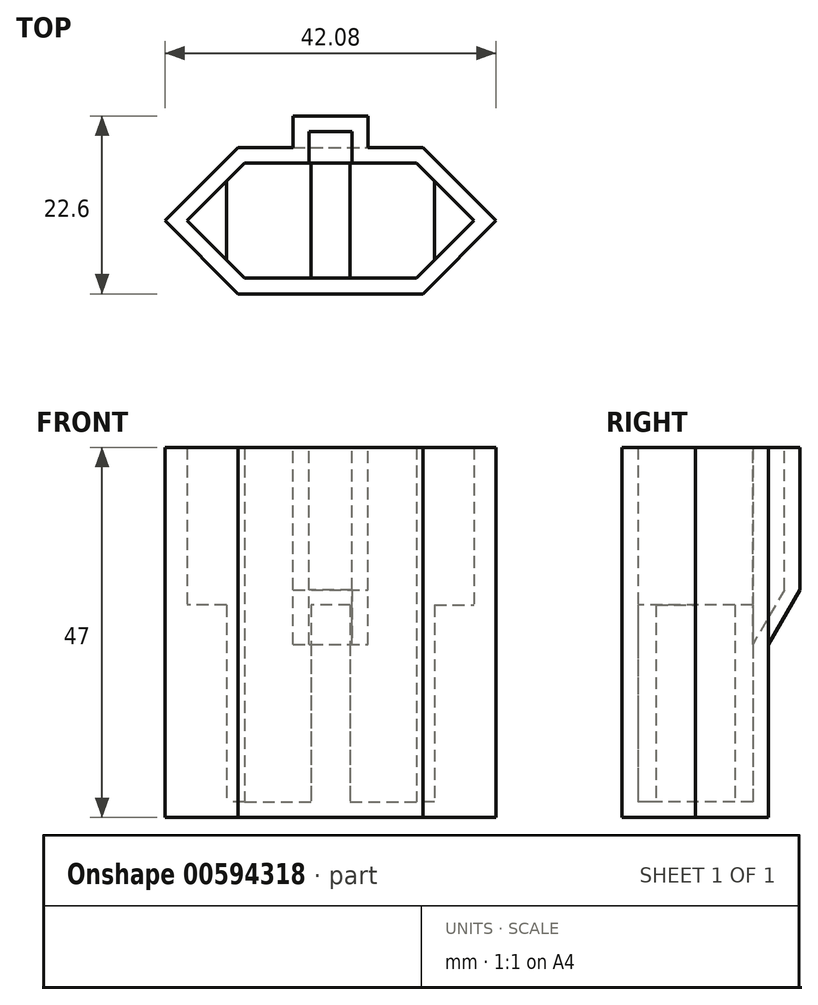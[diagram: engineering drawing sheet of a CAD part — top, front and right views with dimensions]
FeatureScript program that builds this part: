
annotation { "Feature Type Name" : "Feature", "Feature Type Description" : "" }
export const myFeature = defineFeature(function(context is Context, id is Id, definition is map)
    precondition{}
    {
        {
            var Q0;
            Q0=qCreatedBy(makeId("Top.planeOp"),FACE);
            var sketch = newSketch(context, id + "F0", { "sketchPlane" : qUnion([Q0])});
            skLineSegment(sketch, "E0", {"start": v(-10.7, 6.8) * mm, "end": v(10.7, 6.8) * mm, "construction": true});
            skLineSegment(sketch, "E1", {"start": v(10.7, 6.8) * mm, "end": v(17.5, 0) * mm, "construction": true});
            skLineSegment(sketch, "E2", {"start": v(17.5, 0) * mm, "end": v(10.7, -6.8) * mm, "construction": true});
            skLineSegment(sketch, "E3", {"start": v(10.7, -6.8) * mm, "end": v(-10.7, -6.8) * mm, "construction": true});
            skLineSegment(sketch, "E4", {"start": v(-10.7, -6.8) * mm, "end": v(-17.5, 0) * mm, "construction": true});
            skLineSegment(sketch, "E5", {"start": v(-17.5, 0) * mm, "end": v(-10.7, 6.8) * mm, "construction": true});
            skLineSegment(sketch, "E6.0", {"start": v(-10.9, -7.3) * mm, "end": v(-18.2, 0) * mm});
            skLineSegment(sketch, "E6.1", {"start": v(-10.9, 7.3) * mm, "end": v(10.9, 7.3) * mm});
            skLineSegment(sketch, "E6.2", {"start": v(10.9, 7.3) * mm, "end": v(18.2, 0) * mm});
            skLineSegment(sketch, "E6.3", {"start": v(-18.2, 0) * mm, "end": v(-10.9, 7.3) * mm});
            skLineSegment(sketch, "E6.4", {"start": v(18.2, 0) * mm, "end": v(10.9, -7.3) * mm});
            skLineSegment(sketch, "E6.5", {"start": v(10.9, -7.3) * mm, "end": v(-10.9, -7.3) * mm});
            skLineSegment(sketch, "E7.0", {"start": v(-21.04, 0) * mm, "end": v(-11.74, 9.3) * mm});
            skLineSegment(sketch, "E7.1", {"start": v(11.74, 9.3) * mm, "end": v(21.04, 0) * mm});
            skLineSegment(sketch, "E7.2", {"start": v(21.04, 0) * mm, "end": v(11.74, -9.3) * mm});
            skLineSegment(sketch, "E7.3", {"start": v(-11.74, 9.3) * mm, "end": v(11.74, 9.3) * mm});
            skLineSegment(sketch, "E7.4", {"start": v(11.74, -9.3) * mm, "end": v(-11.74, -9.3) * mm});
            skLineSegment(sketch, "E7.5", {"start": v(-11.74, -9.3) * mm, "end": v(-21.04, 0) * mm});
            skSolve(sketch);
        }
        {
            var Q0;
            Q0 = qSketchRegion(id + "F0", true);
            extrude(context, id + "F1", {"entities" : qUnion([Q0]), "depth" : 45 * mm, "offsetDistance" : 25 * mm});
        }
        {
            var Q0;
            Q0=makeQuery(id+"F1.opExtrude","CAP_FACE",FACE,{"disambiguationData":[OSD([sQuery(id+"F0.wireOp",EDGE,"E6.0"),sQuery(id+"F0.wireOp",EDGE,"E6.1"),sQuery(id+"F0.wireOp",EDGE,"E6.2"),sQuery(id+"F0.wireOp",EDGE,"E6.3"),sQuery(id+"F0.wireOp",EDGE,"E6.4"),sQuery(id+"F0.wireOp",EDGE,"E6.5"),sQuery(id+"F0.wireOp",EDGE,"E7.0"),sQuery(id+"F0.wireOp",EDGE,"E7.1"),sQuery(id+"F0.wireOp",EDGE,"E7.2"),sQuery(id+"F0.wireOp",EDGE,"E7.3"),sQuery(id+"F0.wireOp",EDGE,"E7.4"),sQuery(id+"F0.wireOp",EDGE,"E7.5")])],"isStart":false});
            var sketch = newSketch(context, id + "F2", { "sketchPlane" : qUnion([Q0])});
            skLineSegment(sketch, "E8.bottom", {"start": v(-2.75, 9.3) * mm, "end": v(2.75, 9.3) * mm});
            skLineSegment(sketch, "E8.top", {"start": v(-2.75, 7.3) * mm, "end": v(2.75, 7.3) * mm});
            skLineSegment(sketch, "E8.left", {"start": v(-2.75, 9.3) * mm, "end": v(-2.75, 7.3) * mm});
            skLineSegment(sketch, "E8.right", {"start": v(2.75, 9.3) * mm, "end": v(2.75, 7.3) * mm});
            skSolve(sketch);
        }
        {
            var Q0;
            Q0=makeQuery(id+"F2.imprint","IMPRINT",FACE,{"disambiguationData":[TD([[makeQuery(id+"F2.imprint","IMPRINT",EDGE,{"derivedFrom":sQuery(id+"F2.wireOp",EDGE,"E8.top")}),1.0]])]});
            extrude(context, id + "F3", {"entities" : qUnion([Q0]), "operationType" : NewBodyOperationType.REMOVE, "oppositeDirection" : true, "depth" : 25 * mm, "offsetDistance" : 25 * mm});
        }
        {
            var Q0;
            {var subQ3=sQuery(id+"F2.wireOp",EDGE,"E8.left");Q0=makeQuery(id+"F2.imprint","IMPRINT",FACE,{"disambiguationData":[TD([[makeQuery(id+"F2.imprint","IMPRINT",EDGE,{"derivedFrom":subQ3}),-1.0]])]});}
            var sketch = newSketch(context, id + "F4", { "sketchPlane" : qUnion([Q0])});
            skPoint(sketch, "E9.0", {"position": v(2.75, 9.3) * mm});
            skPoint(sketch, "E9.1", {"position": v(-2.75, 9.3) * mm});
            skLineSegment(sketch, "E10", {"start": v(2.75, 9.3) * mm, "end": v(2.75, 11.3) * mm});
            skLineSegment(sketch, "E11", {"start": v(2.75, 11.3) * mm, "end": v(-2.75, 11.3) * mm});
            skLineSegment(sketch, "E12", {"start": v(-2.75, 11.3) * mm, "end": v(-2.75, 9.3) * mm});
            skLineSegment(sketch, "E13", {"start": v(-2.75, 9.3) * mm, "end": v(-4.75, 9.3) * mm});
            skLineSegment(sketch, "E14", {"start": v(-4.75, 9.3) * mm, "end": v(-4.75, 13.3) * mm});
            skLineSegment(sketch, "E15", {"start": v(-4.75, 13.3) * mm, "end": v(4.75, 13.3) * mm});
            skLineSegment(sketch, "E16", {"start": v(4.75, 13.3) * mm, "end": v(4.75, 9.3) * mm});
            skLineSegment(sketch, "E17", {"start": v(4.75, 9.3) * mm, "end": v(2.75, 9.3) * mm});
            skSolve(sketch);
        }
        {
            var Q0;
            Q0 = qSketchRegion(id + "F4", true);
            extrude(context, id + "F5", {"entities" : qUnion([Q0]), "operationType" : NewBodyOperationType.ADD, "oppositeDirection" : true, "depth" : 25 * mm, "offsetDistance" : 25 * mm});
        }
        {
            var Q0;
            Q0=makeQuery(id+"F5.opExtrude","SWEPT_FACE",FACE,{"disambiguationData":[OSD([sQuery(id+"F4.wireOp",EDGE,"E16")])]});
            var sketch = newSketch(context, id + "F6", { "sketchPlane" : qUnion([Q0])});
            skPoint(sketch, "E18.0", {"position": v(9.3, 20) * mm});
            skLineSegment(sketch, "E19", {"start": v(9.3, 20) * mm, "end": v(13.3, 26.93) * mm});
            skSolve(sketch);
        }
        {
            var Q0;
            {var subQ0=sQuery(id+"F6.wireOp",EDGE,"E19");Q0=makeQuery(id+"F6.imprint","IMPRINT",FACE,{"disambiguationData":[TD([[makeQuery(id+"F6.imprint","IMPRINT",EDGE,{"derivedFrom":subQ0}),-1.0]])]});}
            extrude(context, id + "F7", {"entities" : qUnion([Q0]), "operationType" : NewBodyOperationType.REMOVE, "oppositeDirection" : true, "depth" : 25 * mm, "offsetDistance" : 25 * mm});
        }
        {
            var Q0;
            Q0=makeQuery(id+"F5.boolean.opBoolean","MERGE",FACE,{"derivedFrom":[makeQuery(id+"F3.boolean.opBoolean","COPY",FACE,{"derivedFrom":makeQuery(id+"F3.opExtrude","SWEPT_FACE",FACE,{"disambiguationData":[OSD([sQuery(id+"F2.wireOp",EDGE,"E8.left")])]})}),makeQuery(id+"F5.opExtrude","SWEPT_FACE",FACE,{"disambiguationData":[OSD([sQuery(id+"F4.wireOp",EDGE,"E12")])]})]});
            var sketch = newSketch(context, id + "F8", { "sketchPlane" : qUnion([Q0])});
            skLineSegment(sketch, "E20", {"start": v(9.3, 20) * mm, "end": v(7.3, 20) * mm});
            skLineSegment(sketch, "E21", {"start": v(7.3, 20) * mm, "end": v(11.3, 26.93) * mm});
            skLineSegment(sketch, "E22", {"start": v(11.3, 26.93) * mm, "end": v(11.3, 23.46) * mm});
            skLineSegment(sketch, "E23", {"start": v(11.3, 23.46) * mm, "end": v(9.3, 20) * mm});
            skSolve(sketch);
        }
        {
            var Q0;
            Q0 = qSketchRegion(id + "F8", true);
            extrude(context, id + "F9", {"entities" : qUnion([Q0]), "operationType" : NewBodyOperationType.ADD, "endBound" : BoundingType.UP_TO_NEXT, "depth" : 25 * mm, "offsetDistance" : 25 * mm});
        }
        {
            var Q0;
            Q0=makeQuery(id+"F1.opExtrude","CAP_FACE",FACE,{"disambiguationData":[OSD([sQuery(id+"F0.wireOp",EDGE,"E6.0"),sQuery(id+"F0.wireOp",EDGE,"E6.1"),sQuery(id+"F0.wireOp",EDGE,"E6.2"),sQuery(id+"F0.wireOp",EDGE,"E6.3"),sQuery(id+"F0.wireOp",EDGE,"E6.4"),sQuery(id+"F0.wireOp",EDGE,"E6.5"),sQuery(id+"F0.wireOp",EDGE,"E7.0"),sQuery(id+"F0.wireOp",EDGE,"E7.1"),sQuery(id+"F0.wireOp",EDGE,"E7.2"),sQuery(id+"F0.wireOp",EDGE,"E7.3"),sQuery(id+"F0.wireOp",EDGE,"E7.4"),sQuery(id+"F0.wireOp",EDGE,"E7.5")])],"isStart":true});
            var sketch = newSketch(context, id + "F10", { "sketchPlane" : qUnion([Q0])});
            skSolve(sketch);
        }
        {
            var Q0;
            Q0=makeQuery(id+"F10.imprint","IMPRINT",FACE,{"disambiguationData":[TD([[makeQuery(id+"F10.imprint","IMPRINT",EDGE,{"derivedFrom":makeQuery(id+"F1.opExtrude","CAP_EDGE",EDGE,{"disambiguationData":[OSD([sQuery(id+"F0.wireOp",EDGE,"E6.0")])],"isStart":true})}),-1.0]])]});
            var Q1;
            Q1=makeQuery(id+"F10.imprint","IMPRINT",FACE,{"disambiguationData":[TD([[makeQuery(id+"F10.imprint","IMPRINT",EDGE,{"derivedFrom":makeQuery(id+"F1.opExtrude","CAP_EDGE",EDGE,{"disambiguationData":[OSD([sQuery(id+"F0.wireOp",EDGE,"E6.0")])],"isStart":true})}),1.0]])]});
            extrude(context, id + "F11", {"entities" : qUnion([Q0, Q1]), "operationType" : NewBodyOperationType.ADD, "depth" : 2 * mm, "offsetDistance" : 25 * mm});
        }
        {
            var Q0;
            Q0=makeQuery(id+"F11.opExtrude","CAP_FACE",FACE,{"disambiguationData":[OSD([sQuery(id+"F0.wireOp",EDGE,"E7.0"),sQuery(id+"F0.wireOp",EDGE,"E7.1"),sQuery(id+"F0.wireOp",EDGE,"E7.2"),sQuery(id+"F0.wireOp",EDGE,"E7.3"),sQuery(id+"F0.wireOp",EDGE,"E7.4"),sQuery(id+"F0.wireOp",EDGE,"E7.5")])],"isStart":true});
            var sketch = newSketch(context, id + "F12", { "sketchPlane" : qUnion([Q0])});
            skLineSegment(sketch, "E24", {"start": v(13.2, 5) * mm, "end": v(13.2, -5) * mm});
            skLineSegment(sketch, "E25", {"start": v(-13.2, 5) * mm, "end": v(-13.2, -5) * mm});
            skLineSegment(sketch, "E26", {"start": v(13.2, 5) * mm, "end": v(18.2, 0) * mm});
            skLineSegment(sketch, "E27", {"start": v(18.2, 0) * mm, "end": v(13.2, -5) * mm});
            skLineSegment(sketch, "E28", {"start": v(-13.2, 5) * mm, "end": v(-18.2, 0) * mm});
            skLineSegment(sketch, "E29", {"start": v(-18.2, 0) * mm, "end": v(-13.2, -5) * mm});
            skLineSegment(sketch, "E30", {"start": v(2.5, 7.3) * mm, "end": v(2.5, -7.3) * mm});
            skLineSegment(sketch, "E31", {"start": v(-2.5, -7.3) * mm, "end": v(-2.5, 7.3) * mm});
            skLineSegment(sketch, "E32", {"start": v(-2.5, 7.3) * mm, "end": v(2.5, 7.3) * mm});
            skLineSegment(sketch, "E33", {"start": v(2.5, -7.3) * mm, "end": v(-2.5, -7.3) * mm});
            skSolve(sketch);
        }
        {
            var Q0;
            Q0 = qSketchRegion(id + "F12", true);
            extrude(context, id + "F13", {"entities" : qUnion([Q0]), "operationType" : NewBodyOperationType.ADD, "depth" : 25 * mm, "offsetDistance" : 25 * mm});
        }
    });
